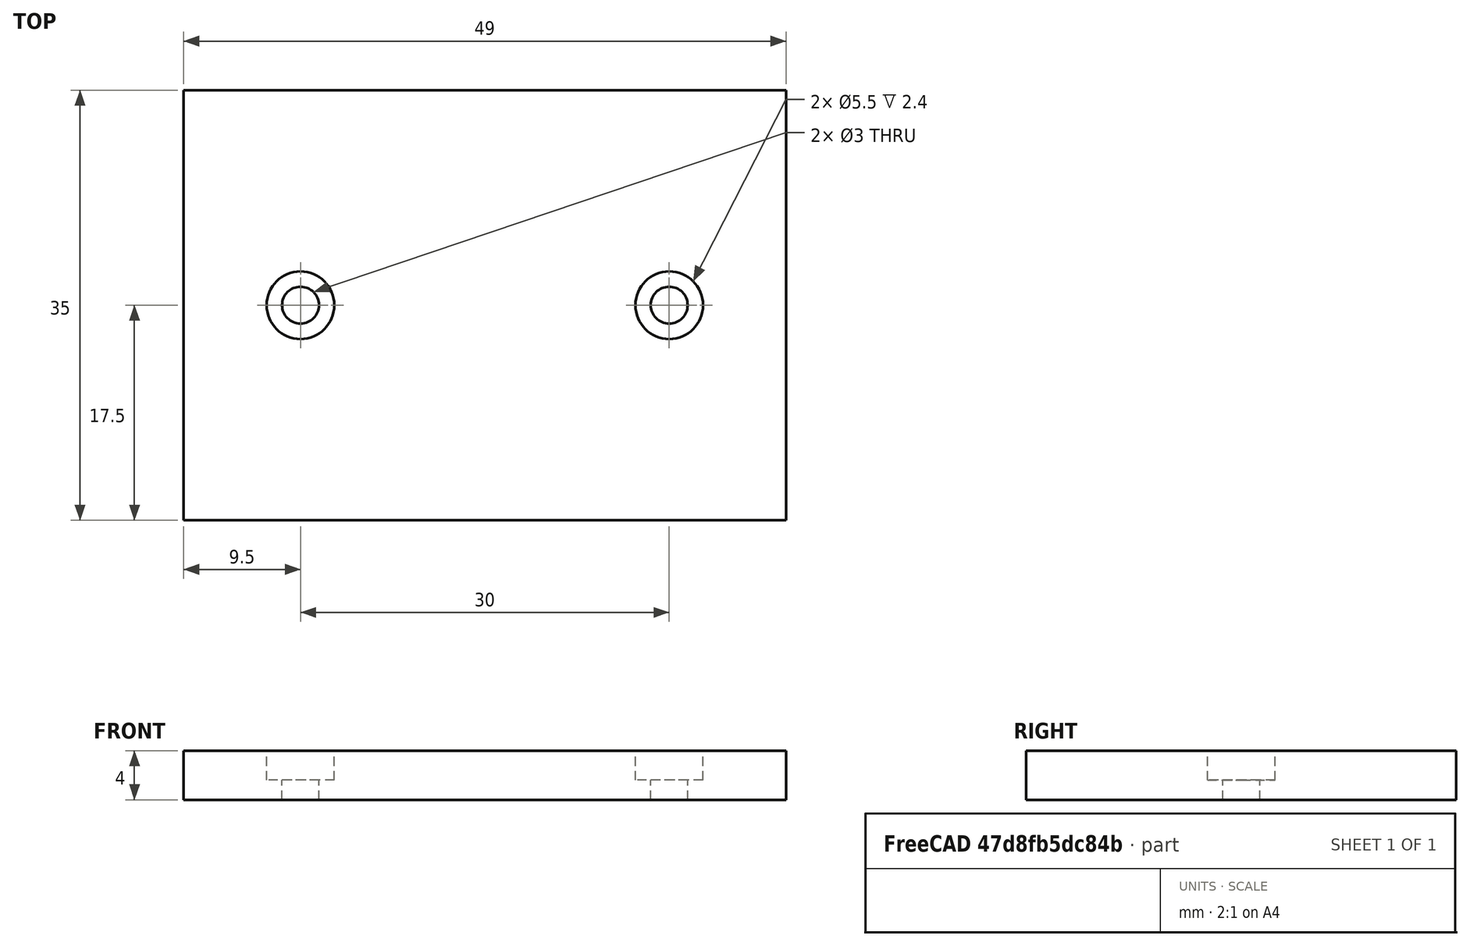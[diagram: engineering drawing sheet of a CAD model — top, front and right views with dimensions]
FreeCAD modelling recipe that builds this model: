
FCSTD DOCUMENT  (FreeCAD 0.18R4 (GitTag))
Label: soporte_mini_breadboard
License: CreativeCommons Attribution-ShareAlike
LicenseURL: http://creativecommons.org/licenses/by-sa/4.0/
objects: Part::Cylinder×4, Part::MultiFuse×2, Part::Cut×2, Part::Box×1
note: 9 computed .brp shape members not serialized (recipe doc carries the construction recipe); baked Part::Feature solids carry a one-line shape summary decoded from their .brp

FEATURE [Part::Box] Box  label="Cube"
  AttacherType = Attacher::AttachEngine3D
  Height = 4
  Length = 49
  Width = 35
FEATURE [Part::Cylinder] Cylinder
  Angle = 360
  AttacherType = Attacher::AttachEngine3D
  Height = 5
  Placement = pos=(0,0,10) rot=(0,0,1;0rad)
  Radius = 1.5
FEATURE [Part::Cylinder] Cylinder001
  Angle = 360
  AttacherType = Attacher::AttachEngine3D
  Height = 3.4
  Placement = pos=(0,0,11.6) rot=(0,0,1;0rad)
  Radius = 2.75
FEATURE [Part::MultiFuse] Fusion
  Placement = pos=(9.5,17.5,-10) rot=(0,0,1;0rad)
  Shapes = -> [Cylinder,Cylinder001]
FEATURE [Part::Cylinder] Cylinder002
  Angle = 360
  AttacherType = Attacher::AttachEngine3D
  Height = 5
  Placement = pos=(0,0,10) rot=(0,0,1;0rad)
  Radius = 1.5
FEATURE [Part::Cylinder] Cylinder003
  Angle = 360
  AttacherType = Attacher::AttachEngine3D
  Height = 3.4
  Placement = pos=(0,0,11.6) rot=(0,0,1;0rad)
  Radius = 2.75
FEATURE [Part::MultiFuse] Fusion001
  Placement = pos=(39.5,17.5,-10) rot=(0,0,1;0rad)
  Shapes = -> [Cylinder002,Cylinder003]
FEATURE [Part::Cut] Cut
  Base = -> Box
  Tool = -> Fusion
FEATURE [Part::Cut] Cut001  label="soporte_para_minibreadboard"
  Base = -> Cut
  Tool = -> Fusion001
